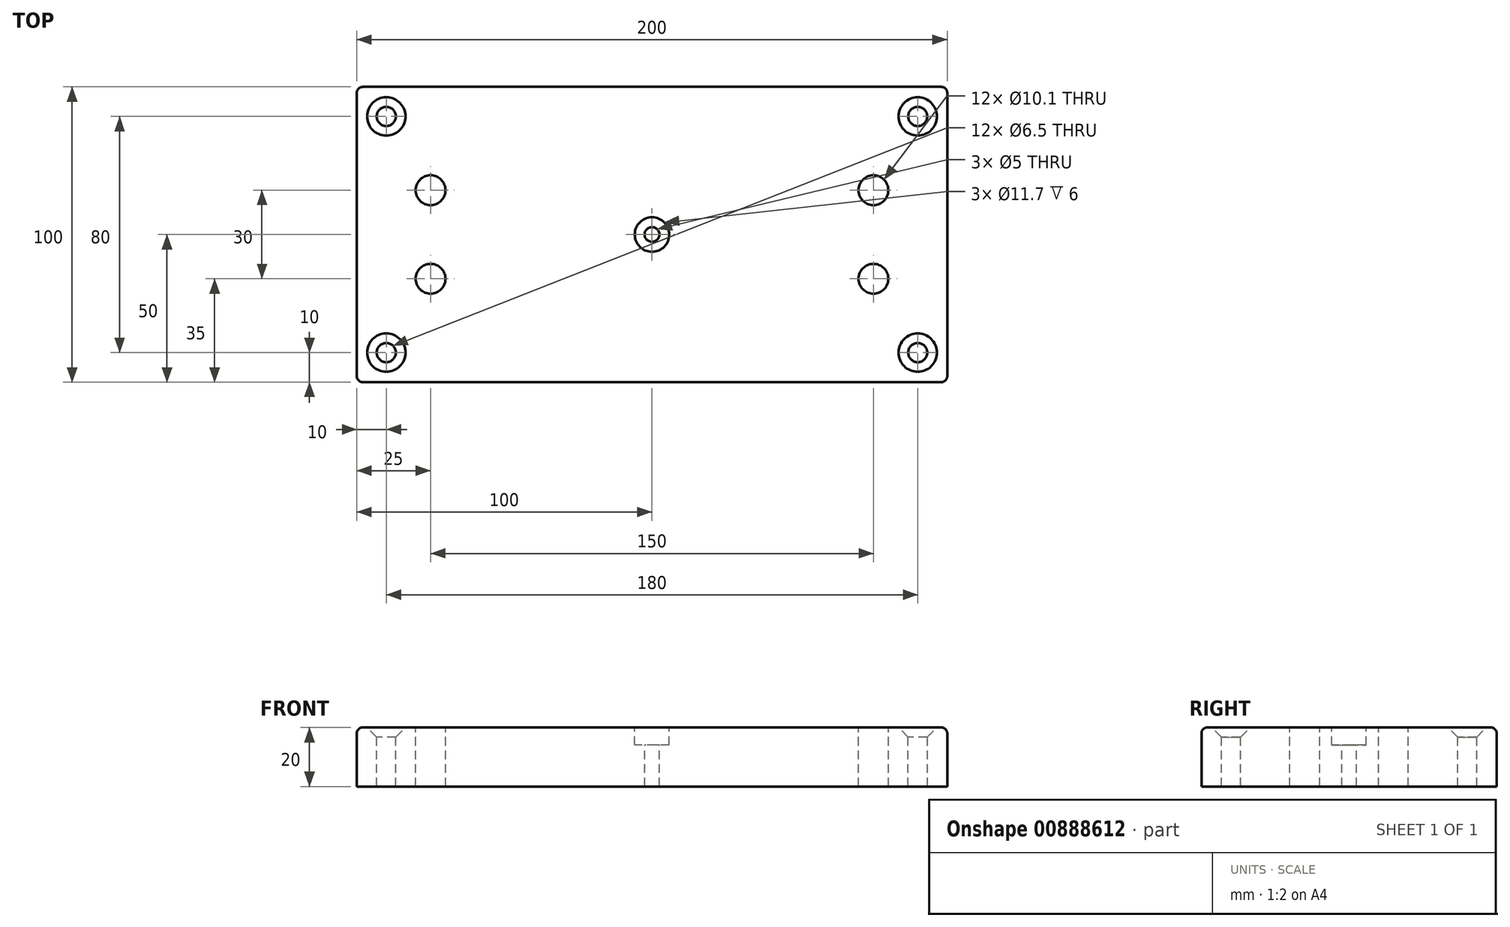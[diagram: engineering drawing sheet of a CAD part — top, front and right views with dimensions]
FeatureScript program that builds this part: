
annotation { "Feature Type Name" : "Feature", "Feature Type Description" : "" }
export const myFeature = defineFeature(function(context is Context, id is Id, definition is map)
    precondition{}
    {
        {
            var Q0;
            Q0=qCreatedBy(makeId("Top.planeOp"),FACE);
            var sketch = newSketch(context, id + "F0", { "sketchPlane" : qUnion([Q0])});
            skLineSegment(sketch, "E0.bottom", {"start": v(100, 50) * mm, "end": v(-100, 50) * mm});
            skLineSegment(sketch, "E0.top", {"start": v(100, -50) * mm, "end": v(-100, -50) * mm});
            skLineSegment(sketch, "E0.left", {"start": v(100, 50) * mm, "end": v(100, -50) * mm});
            skLineSegment(sketch, "E0.right", {"start": v(-100, 50) * mm, "end": v(-100, -50) * mm});
            skPoint(sketch, "E0.middle", {"position": v(0, 0) * mm});
            skSolve(sketch);
        }
        {
            var Q0;
            Q0=makeQuery(id+"F0.imprint","IMPRINT",FACE,{"disambiguationData":[TD([[makeQuery(id+"F0.imprint","IMPRINT",EDGE,{"derivedFrom":sQuery(id+"F0.wireOp",EDGE,"E0.bottom")}),1.0]])]});
            extrude(context, id + "F1", {"entities" : qUnion([Q0]), "depth" : 20 * mm, "offsetDistance" : 25 * mm});
        }
        {
            var Q0;
            Q0=makeQuery(id+"F1.opExtrude","CAP_FACE",FACE,{"disambiguationData":[OSD([sQuery(id+"F0.wireOp",EDGE,"E0.bottom"),sQuery(id+"F0.wireOp",EDGE,"E0.top"),sQuery(id+"F0.wireOp",EDGE,"E0.left"),sQuery(id+"F0.wireOp",EDGE,"E0.right")])],"isStart":false});
            var sketch = newSketch(context, id + "F2", { "sketchPlane" : qUnion([Q0])});
            skLineSegment(sketch, "E1", {"start": v(-75, 50) * mm, "end": v(-75, -50) * mm, "construction": true});
            skLineSegment(sketch, "E2", {"start": v(-100, 15) * mm, "end": v(0, 15) * mm, "construction": true});
            skLineSegment(sketch, "E3", {"start": v(-100, -15) * mm, "end": v(0, -15) * mm, "construction": true});
            skCircle(sketch, "E4", {"center": v(-75, 15) * mm, "radius": 5.05 * mm});
            skCircle(sketch, "E5", {"center": v(-75, -15) * mm, "radius": 5.05 * mm});
            skLineSegment(sketch, "E6.MirrorCS", {"start": v(100, -15) * mm, "end": v(0, -15) * mm, "construction": true});
            skCircle(sketch, "E7.MirrorC", {"center": v(75, -15) * mm, "radius": 5.05 * mm});
            skLineSegment(sketch, "E8.MirrorCS", {"start": v(100, 15) * mm, "end": v(0, 15) * mm, "construction": true});
            skCircle(sketch, "E9.MirrorC", {"center": v(75, 15) * mm, "radius": 5.05 * mm});
            skLineSegment(sketch, "E10.MirrorCS", {"start": v(75, 50) * mm, "end": v(75, -50) * mm, "construction": true});
            skSolve(sketch);
        }
        {
            var Q0;
            Q0 = qSketchRegion(id + "F2", true);
            extrude(context, id + "F3", {"entities" : qUnion([Q0]), "operationType" : NewBodyOperationType.REMOVE, "endBound" : BoundingType.THROUGH_ALL, "oppositeDirection" : true, "depth" : 25 * mm, "offsetDistance" : 25 * mm});
        }
        {
            var Q0;
            Q0=makeQuery(id+"F1.opExtrude","CAP_FACE",FACE,{"disambiguationData":[OSD([sQuery(id+"F0.wireOp",EDGE,"E0.bottom"),sQuery(id+"F0.wireOp",EDGE,"E0.top"),sQuery(id+"F0.wireOp",EDGE,"E0.left"),sQuery(id+"F0.wireOp",EDGE,"E0.right")])],"isStart":false});
            var sketch = newSketch(context, id + "F4", { "sketchPlane" : qUnion([Q0])});
            skCircle(sketch, "E11", {"center": v(-90, 40) * mm, "radius": 0.5 * mm});
            skCircle(sketch, "E12.MirrorC", {"center": v(90, 40) * mm, "radius": 0.5 * mm});
            skCircle(sketch, "E13.MirrorC", {"center": v(-90, -40) * mm, "radius": 0.5 * mm});
            skCircle(sketch, "E14.MirrorC", {"center": v(90, -40) * mm, "radius": 0.5 * mm});
            skSolve(sketch);
        }
        {
            var Q0;
            Q0=sQuery(id+"F4.wireOp",VERTEX,"E11.center");
            var Q1;
            Q1=sQuery(id+"F4.wireOp",VERTEX,"E12.MirrorC.center");
            var Q2;
            Q2=sQuery(id+"F4.wireOp",VERTEX,"E14.MirrorC.center");
            var Q3;
            Q3=sQuery(id+"F4.wireOp",VERTEX,"E13.MirrorC.center");
            var Q4;
            Q4=makeQuery(id+"F1.opExtrude","SWEPT_BODY",BODY,{"disambiguationData":[OSD([sQuery(id+"F0.wireOp",EDGE,"E0.bottom"),sQuery(id+"F0.wireOp",EDGE,"E0.top"),sQuery(id+"F0.wireOp",EDGE,"E0.left"),sQuery(id+"F0.wireOp",EDGE,"E0.right")])]});
            hole(context, id + "F5", {"style" : HoleStyle.C_SINK, "endStyle" : HoleEndStyle.BLIND, "holeDiameter" : 6.5 * mm, "cSinkDiameter" : 13 * mm, "cSinkAngle" : 90 * degree, "majorDiameter" : 5 * mm, "holeDepth" : 25 * mm, "tappedDepth" : 17.6 * mm, "tapClearance" : 3, "startFromSketch" : true, "locations" : qUnion([Q0, Q1, Q2, Q3]), "scope" : qUnion([Q4])});
        }
        {
            var Q0;
            Q0=makeQuery(id+"F1.opExtrude","CAP_FACE",FACE,{"disambiguationData":[OSD([sQuery(id+"F0.wireOp",EDGE,"E0.bottom"),sQuery(id+"F0.wireOp",EDGE,"E0.top"),sQuery(id+"F0.wireOp",EDGE,"E0.left"),sQuery(id+"F0.wireOp",EDGE,"E0.right")])],"isStart":false});
            var sketch = newSketch(context, id + "F6", { "sketchPlane" : qUnion([Q0])});
            skCircle(sketch, "E15", {"center": v(0, 0) * mm, "radius": 3 * mm});
            skSolve(sketch);
        }
        {
            var Q0;
            Q0=sQuery(id+"F6.wireOp",VERTEX,"E15.center");
            var Q1;
            Q1=makeQuery(id+"F1.opExtrude","SWEPT_BODY",BODY,{"disambiguationData":[OSD([sQuery(id+"F0.wireOp",EDGE,"E0.bottom"),sQuery(id+"F0.wireOp",EDGE,"E0.top"),sQuery(id+"F0.wireOp",EDGE,"E0.left"),sQuery(id+"F0.wireOp",EDGE,"E0.right")])]});
            hole(context, id + "F7", {"style" : HoleStyle.SIMPLE, "endStyle" : HoleEndStyle.BLIND, "standardTappedOrClearance" : lookupTablePath({ "standard" : "ISO", "engagement" : "75%", "pitch" : "1 mm", "size" : "M6", "type" : "Tapped" }), "standardBlindInLast" : lookupTablePath({ "standard" : "ISO", "engagement" : "75%", "pitch" : "1 mm", "size" : "M6", "type" : "Tapped" }), "holeDiameter" : 5 * mm, "majorDiameter" : 6 * mm, "showTappedDepth" : true, "holeDepth" : 20 * mm, "tappedDepth" : 17 * mm, "tapClearance" : 3, "startFromSketch" : true, "locations" : qUnion([Q0]), "scope" : qUnion([Q1])});
        }
        {
            var Q0;
            Q0=makeQuery(id+"F1.opExtrude","CAP_FACE",FACE,{"disambiguationData":[OSD([sQuery(id+"F0.wireOp",EDGE,"E0.bottom"),sQuery(id+"F0.wireOp",EDGE,"E0.top"),sQuery(id+"F0.wireOp",EDGE,"E0.left"),sQuery(id+"F0.wireOp",EDGE,"E0.right")])],"isStart":false});
            var sketch = newSketch(context, id + "F8", { "sketchPlane" : qUnion([Q0])});
            skCircle(sketch, "E16", {"center": v(0, 0) * mm, "radius": 5.85 * mm});
            skSolve(sketch);
        }
        {
            var Q0;
            Q0=makeQuery(id+"F8.imprint","IMPRINT",FACE,{"disambiguationData":[TD([[makeQuery(id+"F8.imprint","IMPRINT",EDGE,{"derivedFrom":sQuery(id+"F8.wireOp",EDGE,"E16")}),1.0]])]});
            extrude(context, id + "F9", {"entities" : qUnion([Q0]), "operationType" : NewBodyOperationType.REMOVE, "oppositeDirection" : true, "depth" : 6 * mm, "offsetDistance" : 25 * mm});
        }
        {
            var Q0;
            Q0=makeQuery(id+"F1.opExtrude","SWEPT_EDGE",EDGE,{"disambiguationData":[OSD([sQuery(id+"F0.wireOp",EDGE,"E0.top"),sQuery(id+"F0.wireOp",EDGE,"E0.right")])]});
            var Q1;
            Q1=makeQuery(id+"F1.opExtrude","SWEPT_EDGE",EDGE,{"disambiguationData":[OSD([sQuery(id+"F0.wireOp",EDGE,"E0.top"),sQuery(id+"F0.wireOp",EDGE,"E0.left")])]});
            var Q2;
            Q2=makeQuery(id+"F1.opExtrude","SWEPT_EDGE",EDGE,{"disambiguationData":[OSD([sQuery(id+"F0.wireOp",EDGE,"E0.bottom"),sQuery(id+"F0.wireOp",EDGE,"E0.left")])]});
            var Q3;
            Q3=makeQuery(id+"F1.opExtrude","SWEPT_EDGE",EDGE,{"disambiguationData":[OSD([sQuery(id+"F0.wireOp",EDGE,"E0.bottom"),sQuery(id+"F0.wireOp",EDGE,"E0.right")])]});
            var Q4;
            Q4=makeQuery(id+"F1.opExtrude","CAP_EDGE",EDGE,{"disambiguationData":[OSD([sQuery(id+"F0.wireOp",EDGE,"E0.bottom")])],"isStart":false});
            var Q5;
            Q5=makeQuery(id+"F1.opExtrude","CAP_EDGE",EDGE,{"disambiguationData":[OSD([sQuery(id+"F0.wireOp",EDGE,"E0.left")])],"isStart":false});
            var Q6;
            Q6=makeQuery(id+"F1.opExtrude","CAP_EDGE",EDGE,{"disambiguationData":[OSD([sQuery(id+"F0.wireOp",EDGE,"E0.top")])],"isStart":false});
            var Q7;
            Q7=makeQuery(id+"F1.opExtrude","CAP_EDGE",EDGE,{"disambiguationData":[OSD([sQuery(id+"F0.wireOp",EDGE,"E0.right")])],"isStart":false});
            fillet(context, id + "F10", {"entities" : qUnion([Q0, Q1, Q2, Q3, Q4, Q5, Q6, Q7]), "radius" : 2 * mm, "tangentPropagation" : true, "allowEdgeOverflow" : false});
        }
    });
